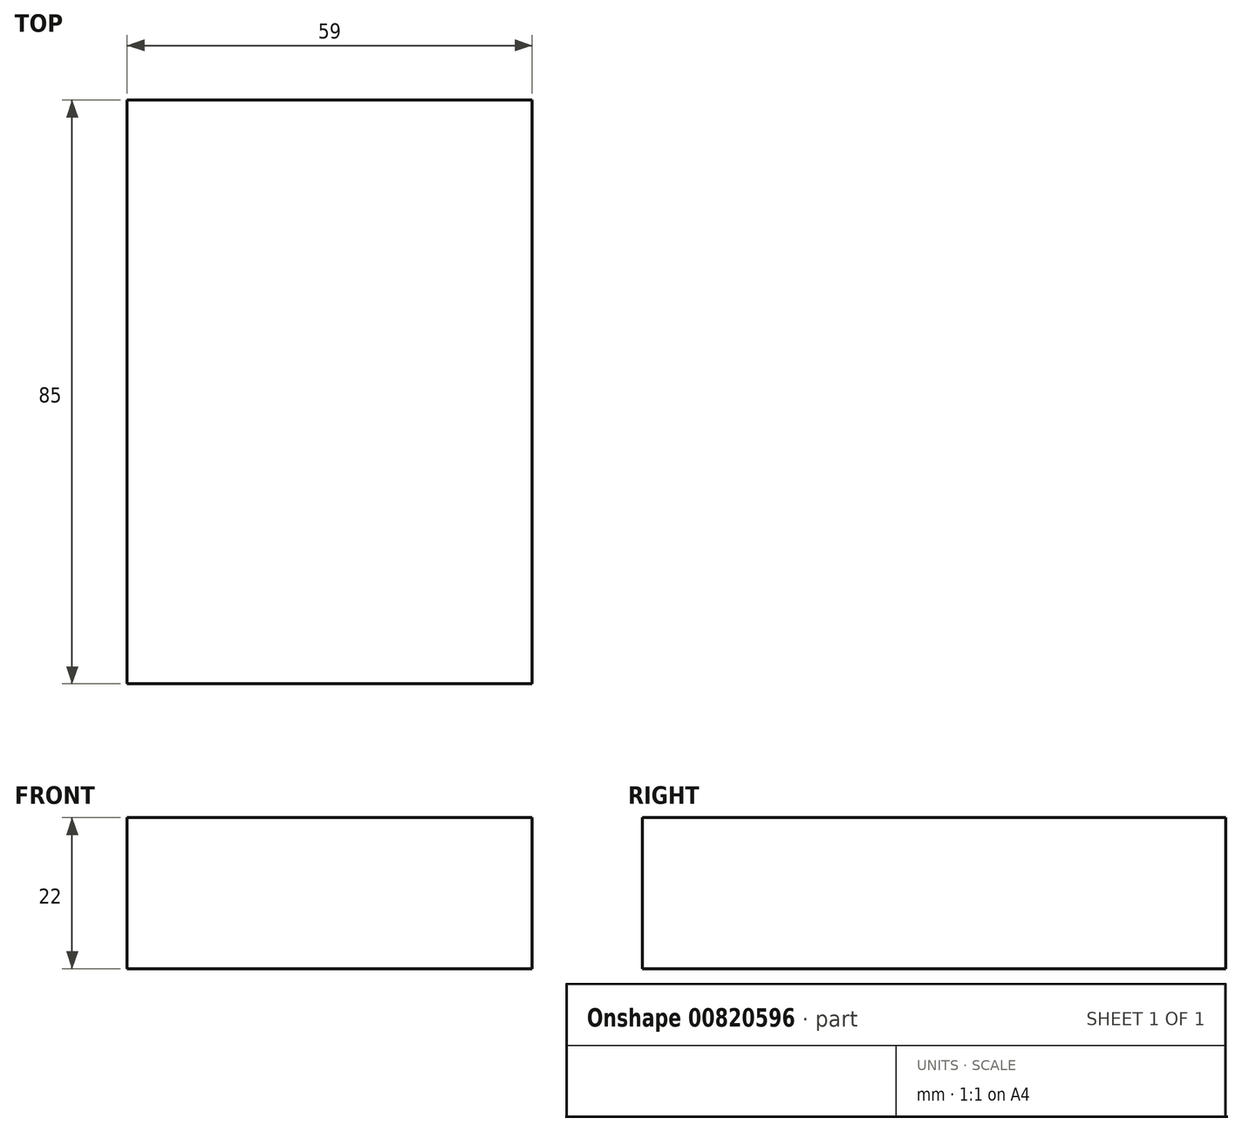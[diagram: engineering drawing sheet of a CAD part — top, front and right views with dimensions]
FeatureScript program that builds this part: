
annotation { "Feature Type Name" : "Feature", "Feature Type Description" : "" }
export const myFeature = defineFeature(function(context is Context, id is Id, definition is map)
    precondition{}
    {
        {
            var Q0;
            Q0=qCreatedBy(makeId("Top.planeOp"),FACE);
            var sketch = newSketch(context, id + "F0", { "sketchPlane" : qUnion([Q0])});
            skLineSegment(sketch, "E0.bottom", {"start": v(-28.58, 43.95) * mm, "end": v(30.42, 43.95) * mm});
            skLineSegment(sketch, "E0.top", {"start": v(-28.58, -41.05) * mm, "end": v(30.42, -41.05) * mm});
            skLineSegment(sketch, "E0.left", {"start": v(-28.58, 43.95) * mm, "end": v(-28.58, -41.05) * mm});
            skLineSegment(sketch, "E0.right", {"start": v(30.42, 43.95) * mm, "end": v(30.42, -41.05) * mm});
            skSolve(sketch);
        }
        {
            var Q0;
            Q0=qSketchRegion(id+"F0",true);
            extrude(context, id + "F1", {"entities" : qUnion([Q0]), "depth" : 22 * mm, "offsetDistance" : 25 * mm});
        }
    });
